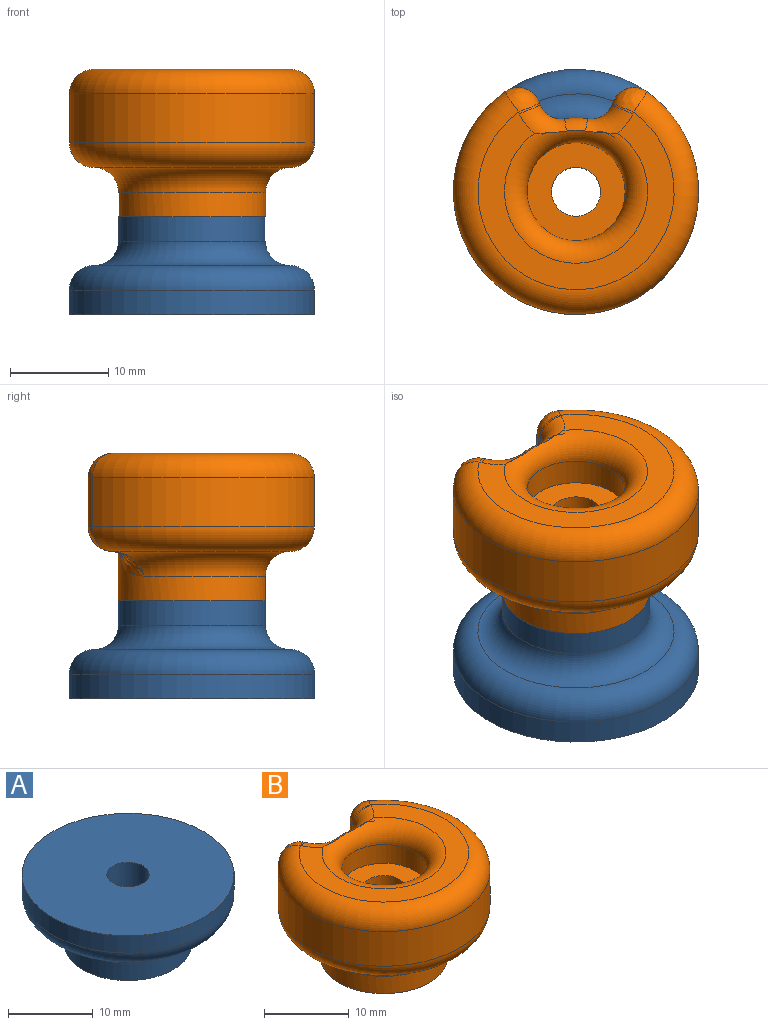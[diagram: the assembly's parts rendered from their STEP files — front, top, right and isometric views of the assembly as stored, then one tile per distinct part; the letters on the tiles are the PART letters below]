
ASSEMBLY  parts=2 mates=1
PART A: 11 faces, bbox 27.1x27.1x10 mm
  f0: cylinder r=2.5mm len=10mm, axis (0,0,1), area 157.1mm2, adj f4,f5
  f1: cylinder r=1.5mm len=5mm, axis (0,0,1), area 47.1mm2, adj f4,f7
  f2: cylinder r=1.5mm len=5mm, axis (0,0,1), area 47.1mm2, adj f4,f8
  f3: cylinder r=7.5mm len=15mm, axis (0,0,1), area 117.8mm2, adj f4,f9
  f4: plane 15x15mm, normal (0,0,-1), area 142.9mm2, adj f0,f1,f2,f3
  f5: plane 25x25mm, normal (0,0,1), area 471.2mm2, adj f0,f6
  f6: cylinder r=12.5mm len=25mm, axis (0,0,-1), area 196.3mm2, adj f5,f10
  f7: plane 3x3mm, normal (0,0,-1), area 7.1mm2, adj f1
  f8: plane 3x3mm, normal (0,0,-1), area 7.1mm2, adj f2
  f9: torus R=10mm, axis (0,0,1), area 207.5mm2, adj f3,f10
  f10: torus R=10mm, axis (0,0,1), area 286mm2, adj f6,f9
PART B: 38 faces, bbox 27.1x25.4x15.1 mm
  f0: bspline ~2.7x2.54mm, area 0mm2, adj f1,f37
  f1: bspline ~4.21x3.75mm, area 10.8mm2, adj f0,f2,f33,f34,f35,f36
  f2: plane 5.4x0.38mm, normal (-0.92,0.38,0), area 2.2mm2, adj f1,f3,f31,f32,f33,f36
  f3: cylinder r=2.3mm len=2.3mm, axis (0.38,0.92,0), area 0.7mm2, adj f2,f4,f30,f32
  f4: plane 20x18.11mm, normal (0,0,1), area 117mm2, adj f3,f5,f27,f28,f29,f30
  f5: torus R=7.3mm, axis (0,0,1), area 126.7mm2, adj f4,f6,f26,f29,f30
  f6: torus R=5.2mm, axis (0,0,1), area 5.6mm2, adj f5,f7,f29,f30
  f7: cylinder r=7.5mm len=15mm, axis (0,0,1), area 150.3mm2, adj f6,f8,f17,f18,f25,f31,f37
  f8: cylinder r=2.3mm len=5.4mm, axis (0,0,1), area 16.6mm2, adj f7,f9,f17,f29
  f9: plane 5.4x0.38mm, normal (0.92,0.38,0), area 2.2mm2, adj f8,f10,f11,f12,f14,f28
  f10: bspline ~2.7x2.54mm, area 0.1mm2, adj f9,f14,f17
  f11: bspline ~4.21x3.75mm, area 10.8mm2, adj f9,f12,f27,f28
  f12: cylinder r=2.3mm len=5mm, axis (0,0,-1), area 20.7mm2, adj f9,f11,f13,f14
  f13: cylinder r=12.5mm len=25mm, axis (0,0,-1), area 315.2mm2, adj f12,f27,f35,f36
  f14: bspline ~4.21x3.75mm, area 10.8mm2, adj f9,f10,f12,f15,f16,f35
  f15: bspline ~2.7x2.54mm, area 0mm2, adj f14,f17
  f16: bspline ~5.07x4.94mm, area 0.8mm2, adj f14,f17,f25
  f17: bspline ~4.8x4.48mm, area 18.1mm2, adj f7,f8,f10,f15,f16
  f18: plane 15x15mm, normal (0,0,-1), area 142.9mm2, adj f7,f19,f21,f23
  f19: cylinder r=1.5mm len=5mm, axis (0,0,-1), area 47.1mm2, adj f18,f20
  f20: plane 3x3mm, normal (0,0,-1), area 7.1mm2, adj f19
  f21: cylinder r=2.5mm len=10mm, axis (0,0,1), area 157.1mm2, adj f18,f22
  f22: plane 10x10mm, normal (0,0,1), area 58.9mm2, adj f21,f26
  f23: cylinder r=1.5mm len=5mm, axis (0,0,-1), area 47.1mm2, adj f18,f24
  f24: plane 3x3mm, normal (0,0,-1), area 7.1mm2, adj f23
  f25: torus R=10mm, axis (0,0,1), area 159.1mm2, adj f7,f16,f34,f35
  f26: cylinder r=5mm len=10mm, axis (0,0,1), area 84.8mm2, adj f5,f22
  f27: torus R=10mm, axis (0,0,1), area 229.3mm2, adj f4,f11,f13,f32
  f28: cylinder r=2.3mm len=2.3mm, axis (0.38,-0.92,0), area 0.7mm2, adj f4,f9,f11,f29
  f29: torus R=4.6mm, axis (0,0,1), area 13.3mm2, adj f4,f5,f6,f8,f28
  f30: torus R=4.6mm, axis (0,0,1), area 13.3mm2, adj f3,f4,f5,f6,f31
  f31: cylinder r=2.3mm len=5.4mm, axis (0,0,1), area 16.6mm2, adj f2,f7,f30,f37
  f32: bspline ~4.21x3.75mm, area 10.8mm2, adj f2,f3,f27,f36
  f33: bspline ~2.7x2.54mm, area 0.1mm2, adj f1,f2,f37
  f34: bspline ~5.07x4.94mm, area 0.8mm2, adj f1,f25,f37
  f35: torus R=10mm, axis (0,0,1), area 229.3mm2, adj f1,f13,f14,f25
  f36: cylinder r=2.3mm len=5mm, axis (0,0,-1), area 20.7mm2, adj f1,f2,f13,f32
  f37: bspline ~5.81x4.48mm, area 18.1mm2, adj f0,f7,f31,f33,f34
PLACE A rot(axis=(0,1,0),180deg) t=(30,0,-10)mm
PLACE B at identity
MATE fastened A.f3 <-> B.f6  axis (0,0,1) through (0,0,-5)mm
